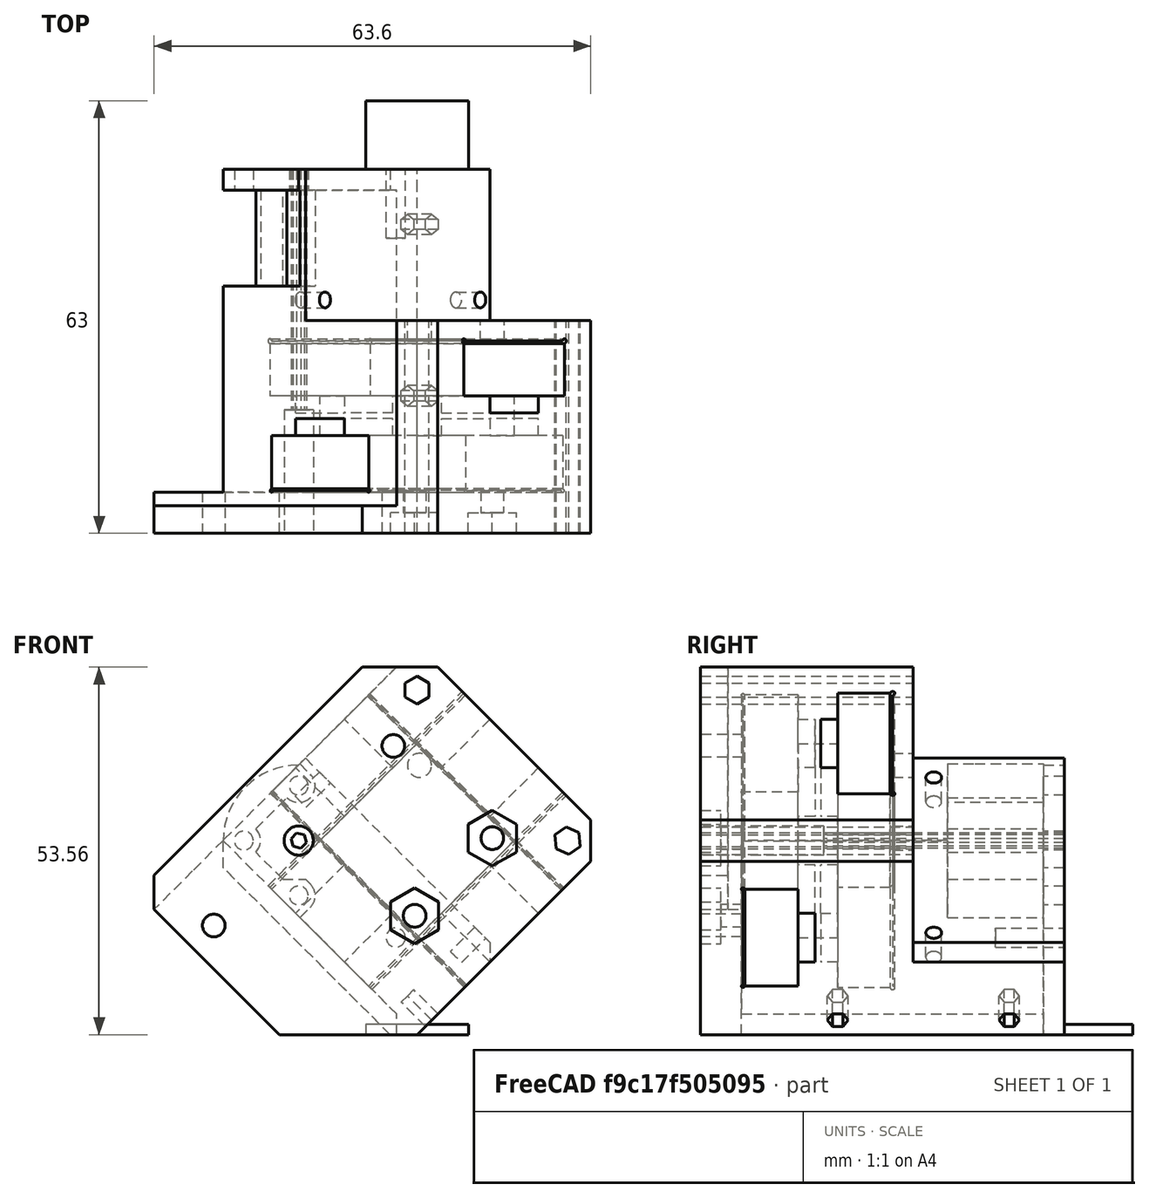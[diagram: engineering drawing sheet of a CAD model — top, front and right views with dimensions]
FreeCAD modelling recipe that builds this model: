
FCSTD DOCUMENT  (FreeCAD 0.19R)
Label: Top
License: All rights reserved
LicenseURL: http://en.wikipedia.org/wiki/All_rights_reserved
objects: Sketcher::SketchObject×25, PartDesign::Pocket×18, PartDesign::Pad×5, PartDesign::Body×1, Mesh::Feature×1
note: 72 computed .brp shape members not serialized (recipe doc carries the construction recipe); baked Part::Feature solids carry a one-line shape summary decoded from their .brp

FEATURE [Sketcher::SketchObject] Sketch  label="Body001"
  FullyConstrained = true
  MapMode = 5
  Support = -> [XY_Plane]
  sketch-geometry (11):
    g0: LineSegment StartX=20 StartY=15.7574 StartZ=0 EndX=20 EndY=-15.7574 EndZ=0
    g1: LineSegment StartX=15.7574 StartY=-20 StartZ=0 EndX=-20 EndY=-20 EndZ=0
    g2: LineSegment StartX=-20 StartY=-15.7574 StartZ=0 EndX=-20 EndY=19.9515 EndZ=0
    g3: Circle CenterX=-12.1976 CenterY=12.1976 CenterZ=0 NormalX=0 NormalY=0 NormalZ=1 AngleXU=0 Radius=2.1
    g4: LineSegment StartX=-12.1976 StartY=12.1976 StartZ=0 EndX=0 EndY=0 EndZ=0
    g5: ArcOfCircle CenterX=-12.1976 CenterY=12.1976 CenterZ=0 NormalX=0 NormalY=0 NormalZ=1 AngleXU=0 Radius=11 StartAngle=0.788519 EndAngle=2.35931
    g6: LineSegment StartX=-4.44373 StartY=20 StartZ=0 EndX=15.7574 EndY=20 EndZ=0
    g7: LineSegment StartX=15.7574 StartY=-20 StartZ=0 EndX=20 EndY=-15.7574 EndZ=0
    g8: LineSegment StartX=-20 StartY=-15.7574 StartZ=0 EndX=-22.1213 EndY=-17.8787 EndZ=0
    g9: LineSegment StartX=-22.1213 StartY=-17.8787 StartZ=0 EndX=-20 EndY=-20 EndZ=0
    g10: LineSegment StartX=15.7574 StartY=20 StartZ=0 EndX=20 EndY=15.7574 EndZ=0
  constraints (32):
    c: Horizontal(g1)
    c: Vertical(g0)
    c: Vertical(g2)
    c: Distance(g-1,g3) = 17.25
    c: Coincident(g4,g3)
    c: Coincident(g4,g-1)
    c: Angle(g4) = -0.785398
    c: Diameter(g3) = 4.2
    c: Coincident(g5,g3)
    c: Diameter(g5) = 22
    c: DistanceX(g1) = -20
    c: Coincident(g6,g5)
    c: Horizontal(g6)
    c: Coincident(g5,g2)
    c: Coincident(g7,g1)
    c: Coincident(g7,g0)
    c: Angle(g7) = 0.785398
    c: Distance(g7) = 6
    c: DistanceY(g1) = -20
    c: Coincident(g2,g8)
    c: Coincident(g8,g9)
    c: Coincident(g9,g1)
    c: Angle(g9) = -0.785398
    c: Angle(g8) = -2.35619
    c: Distance(g9) = 3
    c: DistanceX(g2) = -20
    c: Coincident(g10,g6)
    c: Coincident(g10,g0)
    c: Distance(g10) = 6
    c: Angle(g10) = -0.785398
    c: DistanceX(g0) = 20
    c: DistanceY(g6) = 20
FEATURE [PartDesign::Pad] Pad
  Direction = (1,1,1)
  Length = 53
  Length2 = 10
  Profile = -> Sketch
  Reversed = true
  Type = 0
FEATURE [Sketcher::SketchObject] Sketch001  label="RailHole"
  FullyConstrained = true
  MapMode = 5
  Placement = pos=(20,0,0) rot=(0.57735,0.57735,0.57735;2.0944rad)
  Support = -> [Pad]
  sketch-geometry (10):
    g0: LineSegment StartX=-10.35 StartY=-27.65 StartZ=0 EndX=-10.35 EndY=-20 EndZ=0
    g1: LineSegment StartX=5 StartY=-17.5 StartZ=0 EndX=-5 EndY=-17.5 EndZ=0
    g2: LineSegment StartX=10 StartY=-28 StartZ=0 EndX=-10 EndY=-28 EndZ=0
    g3: LineSegment StartX=5 StartY=-17.5 StartZ=0 EndX=5 EndY=-20 EndZ=0
    g4: LineSegment StartX=-5 StartY=-20 StartZ=0 EndX=-5 EndY=-17.5 EndZ=0
    g5: LineSegment StartX=-10.35 StartY=-20 StartZ=0 EndX=-5 EndY=-20 EndZ=0
    g6: LineSegment StartX=5 StartY=-20 StartZ=0 EndX=10.3495 EndY=-20 EndZ=0
    g7: LineSegment StartX=10.3495 StartY=-27.65 StartZ=0 EndX=10.3495 EndY=-20 EndZ=0
    g8: ArcOfCircle CenterX=-10.35 CenterY=-28 CenterZ=0 NormalX=0 NormalY=0 NormalZ=1 AngleXU=0 Radius=0.35 StartAngle=1.5708 EndAngle=6.28319
    g9: ArcOfCircle CenterX=10.35 CenterY=-28 CenterZ=0 NormalX=0 NormalY=0 NormalZ=1 AngleXU=0 Radius=0.35 StartAngle=3.14159 EndAngle=7.85541
  constraints (29):
    c: Vertical(g0)
    c: Symmetric(g1,g1,g-2)
    c: Distance(g1) = 10
    c: Coincident(g1,g3)
    c: Vertical(g3)
    c: Coincident(g4,g1)
    c: Symmetric(g3,g4,g-2)
    c: Distance(g3) = 2.5
    c: Distance(g2) = 20
    c: Coincident(g5,g4)
    c: Horizontal(g5)
    c: Coincident(g3,g6)
    c: Horizontal(g6)
    c: Vertical(g7)
    c: Coincident(g0,g5)
    c: Coincident(g7,g6)
    c: Coincident(g0,g8)
    c: Coincident(g8,g2)
    c: Diameter(g8) = 0.7
    c: DistanceX(g0,g8) = 0
    c: DistanceY(g2,g8) = 0
    c: Coincident(g9,g2)
    c: Coincident(g9,g7)
    c: Diameter(g9) = 0.7
    c: DistanceY(g2,g9) = 0
    c: DistanceX(g7,g9) = 0.0005
    c: Symmetric(g9,g8,g-2)
    c: Distance(g9,g6) = 8
    c: DistanceY(g8) = -28
FEATURE [PartDesign::Pocket] Pocket
  BaseFeature = -> Pad
  Length = 5
  Length2 = 100
  Profile = -> Sketch001
  Type = 1
FEATURE [Sketcher::SketchObject] Sketch008  label="ExtruderHole"
  FullyConstrained = false
  MapMode = 5
  Placement = pos=(0,0,4) rot=(0,0,1;0rad)
  sketch-geometry (2):
    g0: LineSegment StartX=0 StartY=0 StartZ=0 EndX=-54.6242 EndY=54.6242 EndZ=0
    g1: Circle CenterX=-12.1976 CenterY=12.1976 CenterZ=0 NormalX=0 NormalY=0 NormalZ=1 AngleXU=0 Radius=0.75
  constraints (5):
    c: Coincident(g0,g-1)
    c: Angle(g0) = 2.35619
    c: PointOnObject(g1,g0)
    c: Distance(g-1,g1) = 17.25
    c: Diameter(g1) = 1.5
FEATURE [Sketcher::SketchObject] Sketch009  label="reference"
  FullyConstrained = false
  MapMode = 5
  Placement = pos=(0,0,-25) rot=(1,0,0;3.14159rad)
  sketch-geometry (2):
    g0: Circle CenterX=-12.0208 CenterY=-12.0208 CenterZ=0 NormalX=0 NormalY=0 NormalZ=1 AngleXU=0 Radius=10
    g1: LineSegment StartX=0 StartY=0 StartZ=0 EndX=-27.7674 EndY=-27.7674 EndZ=0
  constraints (5):
    c: Diameter(g0) = 20
    c: Coincident(g1,g-1)
    c: Angle(g1) = -2.35619
    c: PointOnObject(g0,g1)
    c: Distance(g0,g1) = 17
FEATURE [Sketcher::SketchObject] Sketch010  label="reference2"
  FullyConstrained = false
  MapMode = 5
  Placement = pos=(0,0,-37) rot=(1,0,0;3.14159rad)
  sketch-geometry (2):
    g0: Circle CenterX=-12.1976 CenterY=-12.1976 CenterZ=0 NormalX=0 NormalY=0 NormalZ=1 AngleXU=0 Radius=8
    g1: LineSegment StartX=0 StartY=0 StartZ=0 EndX=-38.1566 EndY=-38.1566 EndZ=0
  constraints (5):
    c: Diameter(g0) = 16
    c: Coincident(g1,g-1)
    c: Angle(g1) = -2.35619
    c: Distance(g0,g1) = 17.25
    c: PointOnObject(g0,g1)
FEATURE [Sketcher::SketchObject] Sketch021  label="InternalTri"
  FullyConstrained = true
  MapMode = 5
  Placement = pos=(0,-3e-15,-12) rot=(0,0,1;0rad)
  sketch-geometry (4):
    g0: LineSegment StartX=-10 StartY=10 StartZ=0 EndX=10 EndY=10 EndZ=0
    g1: LineSegment StartX=10 StartY=10 StartZ=0 EndX=10 EndY=-10 EndZ=0
    g2: LineSegment StartX=10 StartY=-10 StartZ=0 EndX=-10 EndY=-10 EndZ=0
    g3: LineSegment StartX=-10 StartY=-10 StartZ=0 EndX=-10 EndY=10 EndZ=0
  constraints (11):
    c: Coincident(g0,g1)
    c: Coincident(g1,g2)
    c: Coincident(g2,g3)
    c: Coincident(g3,g0)
    c: Horizontal(g0)
    c: Horizontal(g2)
    c: Vertical(g1)
    c: Vertical(g3)
    c: Symmetric(g1,g0,g-1)
    c: Equal(g1,g0)
    c: Distance(g1) = 20
FEATURE [PartDesign::Pocket] Pocket002
  BaseFeature = -> Pocket
  Length = 10
  Length2 = 2
  Profile = -> Sketch021
  Type = 4
FEATURE [Sketcher::SketchObject] Sketch019  label="RailHole2"
  FullyConstrained = true
  MapMode = 5
  Placement = pos=(0,-20,0) rot=(1,0,0;1.5708rad)
  Support = -> [Pocket002]
  sketch-geometry (10):
    g0: LineSegment StartX=-9.75 StartY=-6.2 StartZ=0 EndX=9.75 EndY=-6.2 EndZ=0
    g1: LineSegment StartX=10 StartY=-14.2 StartZ=0 EndX=5 EndY=-14.2 EndZ=0
    g2: LineSegment StartX=5 StartY=-14.2 StartZ=0 EndX=5 EndY=-16.7 EndZ=0
    g3: LineSegment StartX=5 StartY=-16.7 StartZ=0 EndX=-5 EndY=-16.7 EndZ=0
    g4: LineSegment StartX=-5 StartY=-16.7 StartZ=0 EndX=-5 EndY=-14.2 EndZ=0
    g5: LineSegment StartX=-5 StartY=-14.2 StartZ=0 EndX=-10 EndY=-14.2 EndZ=0
    g6: ArcOfCircle CenterX=10 CenterY=-6.2 CenterZ=0 NormalX=0 NormalY=0 NormalZ=1 AngleXU=0 Radius=0.25 StartAngle=4.71239 EndAngle=9.42478
    g7: ArcOfCircle CenterX=-10 CenterY=-6.2 CenterZ=0 NormalX=0 NormalY=0 NormalZ=1 AngleXU=0 Radius=0.25 StartAngle=-9e-16 EndAngle=4.71239
    g8: LineSegment StartX=-10 StartY=-14.2 StartZ=0 EndX=-10 EndY=-6.45 EndZ=0
    g9: LineSegment StartX=10 StartY=-14.2 StartZ=0 EndX=10 EndY=-6.45 EndZ=0
  constraints (29):
    c: Horizontal(g0)
    c: Horizontal(g1)
    c: Coincident(g1,g2)
    c: Vertical(g2)
    c: Coincident(g2,g3)
    c: Horizontal(g3)
    c: Coincident(g3,g4)
    c: Vertical(g4)
    c: Coincident(g4,g5)
    c: Symmetric(g1,g5,g-2)
    c: Distance(g3) = 10
    c: Symmetric(g4,g1,g-2)
    c: DistanceY(g0) = -6.2
    c: Distance(g2) = 2.5
    c: Coincident(g6,g0)
    c: Coincident(g7,g0)
    c: Distance(g7,g6) = 20
    c: DistanceY(g1,g6) = 8
    c: Coincident(g8,g5)
    c: Vertical(g8)
    c: Coincident(g9,g1)
    c: Coincident(g9,g6)
    c: Vertical(g9)
    c: Coincident(g7,g8)
    c: Symmetric(g6,g7,g-2)
    c: Diameter(g6) = 0.5
    c: Equal(g6,g7)
    c: DistanceX(g7,g7) = 0
    c: DistanceY(g7,g0) = 0
FEATURE [Sketcher::SketchObject] Sketch024  label="hgxLITEholes"
  FullyConstrained = false
  MapMode = 5
  Placement = pos=(0,0,4) rot=(0,0,1;0rad)
  sketch-geometry (5):
    g0: Circle CenterX=7.30241 CenterY=12.1976 CenterZ=0 NormalX=0 NormalY=0 NormalZ=1 AngleXU=0 Radius=1.65
    g1: Circle CenterX=-29.6976 CenterY=12.1976 CenterZ=0 NormalX=0 NormalY=0 NormalZ=1 AngleXU=0 Radius=1.65
    g2: LineSegment StartX=-29.6976 StartY=12.1976 StartZ=0 EndX=7.30241 EndY=12.1976 EndZ=0
    g3: LineSegment StartX=0 StartY=0 StartZ=0 EndX=-27.1729 EndY=27.1729 EndZ=0
    g4: Circle CenterX=-12.1976 CenterY=12.1976 CenterZ=0 NormalX=0 NormalY=0 NormalZ=1 AngleXU=0 Radius=1.0154
  constraints (12):
    c: Diameter(g0) = 3.3
    c: Equal(g0,g1)
    c: Coincident(g2,g1)
    c: Coincident(g2,g0)
    c: Distance(g2) = 37
    c: Coincident(g3,g-1)
    c: Angle(g3) = 2.35619
    c: PointOnObject(g4,g3)
    c: Distance(g-1,g4) = 17.25
    c: Distance(g4,g0) = 19.5
    c: Horizontal(g2)
    c: PointOnObject(g4,g2)
FEATURE [PartDesign::Pocket] Pocket003
  BaseFeature = -> Pocket002
  Length = 5
  Length2 = 100
  Profile = -> Sketch019
  Type = 1
FEATURE [Sketcher::SketchObject] Sketch026  label="BottomSculp"
  FullyConstrained = false
  MapMode = 5
  Placement = pos=(0,0,-53) rot=(1,0,0;3.14159rad)
  Support = -> [Pocket003]
  sketch-geometry (5):
    g0: LineSegment StartX=29.4648 StartY=27.8981 StartZ=0 EndX=28.2209 EndY=-23.4245 EndZ=0
    g1: LineSegment StartX=28.2209 StartY=-23.4245 StartZ=0 EndX=-3.00001 EndY=-23.4245 EndZ=0
    g2: LineSegment StartX=-3.00001 StartY=-23.4245 StartZ=0 EndX=-3 EndY=18 EndZ=0
    g3: LineSegment StartX=-3 StartY=18 StartZ=0 EndX=-14.2101 EndY=29.2101 EndZ=0
    g4: LineSegment StartX=-14.2101 StartY=29.2101 StartZ=0 EndX=29.4648 EndY=27.8981 EndZ=0
  constraints (11):
    c: Coincident(g0,g1)
    c: Horizontal(g1)
    c: Coincident(g1,g2)
    c: Angle(g2) = 1.5708
    c: Coincident(g2,g3)
    c: Angle(g3) = 2.35619
    c: Coincident(g4,g3)
    c: Coincident(g4,g0)
    c: DistanceY(g2) = 18
    c: DistanceX(g2) = -3
    c: Angle(g3) = 2.35619
FEATURE [PartDesign::Pocket] Pocket004
  BaseFeature = -> Pocket003
  Length = 22
  Length2 = 100
  Profile = -> Sketch026
  Type = 0
FEATURE [Sketcher::SketchObject] Sketch004  label="Yboltpattern"
  FullyConstrained = true
  MapMode = 5
  Placement = pos=(0,0,-31) rot=(1,0,0;3.14159rad)
  Support = -> [Pocket004]
  sketch-geometry (8):
    g0: Circle CenterX=-8 CenterY=7.5 CenterZ=0 NormalX=0 NormalY=0 NormalZ=1 AngleXU=0 Radius=1.75
    g1: Circle CenterX=8 CenterY=7.5 CenterZ=0 NormalX=0 NormalY=0 NormalZ=1 AngleXU=0 Radius=1.75
    g2: Circle CenterX=-8 CenterY=-7.5 CenterZ=0 NormalX=0 NormalY=0 NormalZ=1 AngleXU=0 Radius=1.75
    g3: Circle CenterX=8 CenterY=-7.5 CenterZ=0 NormalX=0 NormalY=0 NormalZ=1 AngleXU=0 Radius=1.75
    g4: LineSegment StartX=-8 StartY=7.5 StartZ=0 EndX=8 EndY=7.5 EndZ=0
    g5: LineSegment StartX=8 StartY=7.5 StartZ=0 EndX=8 EndY=-7.5 EndZ=0
    g6: LineSegment StartX=8 StartY=-7.5 StartZ=0 EndX=-8 EndY=-7.5 EndZ=0
    g7: LineSegment StartX=-8 StartY=-7.5 StartZ=0 EndX=-8 EndY=7.5 EndZ=0
  constraints (18):
    c: Diameter(g0) = 3.5
    c: Equal(g0,g1)
    c: Equal(g0,g2)
    c: Equal(g0,g3)
    c: Distance(g2,g0) = 15
    c: Distance(g3,g2) = 16
    c: Coincident(g4,g0)
    c: Coincident(g4,g1)
    c: Coincident(g4,g5)
    c: Coincident(g5,g3)
    c: Coincident(g5,g6)
    c: Coincident(g6,g2)
    c: Coincident(g6,g7)
    c: Coincident(g7,g4)
    c: Equal(g5,g7)
    c: Equal(g4,g6)
    c: Symmetric(g1,g2,g-1)
    c: Symmetric(g0,g1,g-2)
FEATURE [Sketcher::SketchObject] Sketch022  label="VoronHoleRelif"
  FullyConstrained = true
  MapMode = 5
  Placement = pos=(0,0,-28) rot=(0,0,1;0rad)
  Support = -> [Pocket004]
  sketch-geometry (11):
    g0: ArcOfCircle CenterX=-17.8884 CenterY=6.52425 CenterZ=0 NormalX=0 NormalY=0 NormalZ=1 AngleXU=0 Radius=2.4 StartAngle=4.71239 EndAngle=6.28319
    g1: ArcOfCircle CenterX=-6.58192 CenterY=17.8307 CenterZ=0 NormalX=0 NormalY=0 NormalZ=1 AngleXU=0 Radius=2.4 StartAngle=3.14159 EndAngle=6.28319
    g2: LineSegment StartX=-22.2684 StartY=4.12425 StartZ=0 EndX=-17.8884 EndY=4.12425 EndZ=0
    g3: LineSegment StartX=-22.2684 StartY=23.8307 StartZ=0 EndX=-4.18192 EndY=23.8307 EndZ=0
    g4: LineSegment StartX=-4.18192 StartY=23.8307 StartZ=0 EndX=-4.18192 EndY=17.8307 EndZ=0
    g5: LineSegment StartX=-22.2684 StartY=4.12425 StartZ=0 EndX=-22.2684 EndY=23.8307 EndZ=0
    g6: ArcOfCircle CenterX=-17.8172 CenterY=17.8307 CenterZ=0 NormalX=0 NormalY=0 NormalZ=1 AngleXU=0 Radius=2.4 StartAngle=4.71239 EndAngle=6.28319
    g7: LineSegment StartX=-15.4172 StartY=17.8307 StartZ=0 EndX=-8.98192 EndY=17.8307 EndZ=0
    g8: LineSegment StartX=-17.8172 StartY=9.85307 StartZ=0 EndX=-15.4884 EndY=7.52425 EndZ=0
    g9: LineSegment StartX=-15.4884 StartY=6.52425 StartZ=0 EndX=-15.4884 EndY=7.52425 EndZ=0
    g10: LineSegment StartX=-17.8172 StartY=9.85307 StartZ=0 EndX=-17.8172 EndY=15.4307 EndZ=0
  constraints (33):
    c: Horizontal(g2)
    c: Coincident(g3,g4)
    c: Tangent(g4,g1) = 1.5708
    c: Tangent(g2,g0) = -1.5708
    c: Diameter(g0) = 4.8
    c: Equal(g0,g1)
    c: Vertical(g4)
    c: Horizontal(g3)
    c: Coincident(g5,g2)
    c: Coincident(g5,g3)
    c: Vertical(g5)
    c: Distance(g2) = 4.38
    c: Distance(g4) = 6
    c: DistanceX(g1) = -6.58192
    c: DistanceY(g1) = 17.8307
    c: DistanceX(g0) = -17.8884
    c: DistanceY(g0) = 6.52425
    c: Coincident(g7,g6)
    c: Coincident(g7,g1)
    c: Horizontal(g7)
    c: Perpendicular(g1,g7)
    c: Diameter(g6) = 4.8
    c: Perpendicular(g6,g7)
    c: Angle(g8) = -0.785398
    c: Vertical(g9)
    c: Tangent(g9,g0) = -1.5708
    c: Distance(g9) = 1
    c: Coincident(g8,g9)
    c: Coincident(g10,g8)
    c: Coincident(g10,g6)
    c: Vertical(g10)
    c: Perpendicular(g6,g10)
    c: DistanceX(g6) = -17.8172
FEATURE [PartDesign::Pocket] Pocket005
  BaseFeature = -> Pocket004
  Length = 22
  Length2 = -8
  Profile = -> Sketch022
  Type = 4
FEATURE [Sketcher::SketchObject] Sketch017  label="VoronHoles3"
  FullyConstrained = true
  MapMode = 5
  Placement = pos=(0,0,-50) rot=(0,0,1;0rad)
  Support = -> [Pocket005]
  sketch-geometry (10):
    g0: Circle CenterX=-6.54074 CenterY=17.8544 CenterZ=0 NormalX=0 NormalY=0 NormalZ=1 AngleXU=0 Radius=1.375
    g1: Circle CenterX=-17.8544 CenterY=6.54074 CenterZ=0 NormalX=0 NormalY=0 NormalZ=1 AngleXU=0 Radius=1.375
    g2: Circle CenterX=-6.54074 CenterY=6.54074 CenterZ=0 NormalX=0 NormalY=0 NormalZ=1 AngleXU=0 Radius=1.375
    g3: Circle CenterX=-17.8544 CenterY=17.8544 CenterZ=0 NormalX=0 NormalY=0 NormalZ=1 AngleXU=0 Radius=1.375
    g4: LineSegment StartX=-6.54074 StartY=17.8544 StartZ=0 EndX=-6.54074 EndY=6.54074 EndZ=0
    g5: LineSegment StartX=-6.54074 StartY=6.54074 StartZ=0 EndX=-17.8544 EndY=6.54074 EndZ=0
    g6: LineSegment StartX=-17.8544 StartY=6.54074 StartZ=0 EndX=-17.8544 EndY=17.8544 EndZ=0
    g7: LineSegment StartX=-17.8544 StartY=17.8544 StartZ=0 EndX=-6.54074 EndY=17.8544 EndZ=0
    g8: LineSegment StartX=0 StartY=0 StartZ=0 EndX=-37.1726 EndY=37.1726 EndZ=0
    g9: Circle CenterX=-12.1976 CenterY=12.1976 CenterZ=0 NormalX=0 NormalY=0 NormalZ=1 AngleXU=0 Radius=0.77
  constraints (25):
    c: Coincident(g4,g0)
    c: Coincident(g4,g2)
    c: Coincident(g4,g5)
    c: Coincident(g5,g1)
    c: Coincident(g5,g6)
    c: Coincident(g6,g3)
    c: Coincident(g6,g7)
    c: Coincident(g7,g4)
    c: Equal(g4,g7)
    c: Equal(g7,g6)
    c: Equal(g6,g5)
    c: Coincident(g8,g-1)
    c: PointOnObject(g9,g8)
    c: Distance(g-1,g9) = 17.25
    c: Diameter(g1) = 2.75
    c: Equal(g1,g3)
    c: Equal(g1,g0)
    c: Equal(g1,g2)
    c: Symmetric(g0,g1,g9)
    c: Distance(g2,g3) = 16
    c: Angle(g8) = 2.35619
    c: PointOnObject(g2,g8)
    c: Perpendicular(g7,g4)
    c: Distance(g8) = 52.57
    c: Diameter(g9) = 1.54
FEATURE [PartDesign::Pocket] Pocket006
  BaseFeature = -> Pocket005
  Length = 5
  Length2 = 100
  Profile = -> Sketch017
  Type = 1
FEATURE [Sketcher::SketchObject] Sketch025  label="FanDuctMountHole"
  FullyConstrained = true
  MapMode = 5
  Placement = pos=(0,0,-53) rot=(1,0,0;3.14159rad)
  Support = -> [Pocket006]
  sketch-geometry (1):
    g0: Circle CenterX=-12.2 CenterY=7.8 CenterZ=0 NormalX=0 NormalY=0 NormalZ=1 AngleXU=0 Radius=1.4
  constraints (3):
    c: Diameter(g0) = 2.8
    c: DistanceX(g0) = -12.2
    c: DistanceY(g0) = 7.8
FEATURE [PartDesign::Pocket] Pocket007
  BaseFeature = -> Pocket006
  Length = 10
  Length2 = 100
  Profile = -> Sketch025
  Type = 0
FEATURE [PartDesign::Pocket] Pocket008
  BaseFeature = -> Pocket007
  Length = 9
  Length2 = 100
  Profile = -> Sketch004
  Type = 0
FEATURE [Sketcher::SketchObject] Sketch007  label="ExtruderPlatform"
  ExternalGeometry = -> [Pad]
  FullyConstrained = false
  MapMode = 5
  Support = -> [Pocket008]
  sketch-geometry (12):
    g0: LineSegment StartX=-20 StartY=-20 StartZ=0 EndX=15.7574 EndY=-20 EndZ=0
    g1: LineSegment StartX=0 StartY=0 StartZ=0 EndX=-70.7107 EndY=70.7107 EndZ=0
    g2: Circle CenterX=-12.1976 CenterY=12.1976 CenterZ=0 NormalX=0 NormalY=0 NormalZ=1 AngleXU=0 Radius=2.125
    g3: LineSegment StartX=15.7574 StartY=-20 StartZ=0 EndX=20 EndY=-15.7574 EndZ=0
    g4: LineSegment StartX=20 StartY=-15.7574 StartZ=0 EndX=20 EndY=15.7574 EndZ=0
    g5: LineSegment StartX=20 StartY=15.7574 StartZ=0 EndX=15.7574 EndY=20 EndZ=0
    g6: LineSegment StartX=-20 StartY=-20 StartZ=0 EndX=-34.1976 EndY=-5.80241 EndZ=0
    g7: LineSegment StartX=-12.1976 StartY=-100 StartZ=0 EndX=-12.1976 EndY=100 EndZ=0
    g8: LineSegment StartX=-34.1976 StartY=-5.80241 StartZ=0 EndX=-34.1976 EndY=20 EndZ=0
    g9: LineSegment StartX=-34.1976 StartY=20 StartZ=0 EndX=15.7574 EndY=20 EndZ=0
    g10: Circle CenterX=-29.6976 CenterY=12.1976 CenterZ=0 NormalX=0 NormalY=0 NormalZ=1 AngleXU=0 Radius=1.4
    g11: Circle CenterX=7.30241 CenterY=11.9057 CenterZ=0 NormalX=0 NormalY=0 NormalZ=1 AngleXU=0 Radius=1.4
  constraints (35):
    c: Coincident(g1,g-1)
    c: Angle(g1) = 2.35619
    c: Diameter(g2) = 4.25
    c: PointOnObject(g2,g1)
    c: Distance(g-1,g2) = 17.25
    c: Coincident(g0,g3)
    c: Coincident(g3,g4)
    c: Coincident(g6,g0)
    c: Angle(g6) = 2.35619
    c: Coincident(g5,g4)
    c: Distance(g1) = 100
    c: PointOnObject(g2,g7)
    c: DistanceX(g0,g0) = -35.7574
    c: DistanceY(g0,g0) = 0
    c: DistanceX(g3,g0) = -40
    c: DistanceY(g3,g0) = -4.24264
    c: DistanceX(g4) = 20
    c: DistanceY(g4) = 15.7574
    c: DistanceX(g3) = 20
    c: DistanceY(g3) = -15.7574
    c: Coincident(g8,g6)
    c: Vertical(g8)
    c: Horizontal(g9)
    c: Coincident(g5,g9)
    c: Distance(g8,g7) = 22
    c: DistanceX(g5) = 15.7574
    c: DistanceY(g5) = 20
    c: Symmetric(g7,g7,g-1)
    c: Distance(g7) = 200
    c: DistanceX(g10,g2) = 17.5
    c: DistanceX(g2,g11) = 19.5
    c: Diameter(g10) = 2.8
    c: Equal(g10,g11)
    c: DistanceY(g10,g2) = 0
    c: Coincident(g9,g8)
FEATURE [PartDesign::Pad] Pad001
  BaseFeature = -> Pocket008
  Direction = (1,1,1)
  Length = 6
  Length2 = 100
  Profile = -> Sketch007
  Reversed = true
  Type = 0
FEATURE [PartDesign::Pocket] Pocket009
  BaseFeature = -> Pad001
  Length = 11
  Length2 = 100
  Profile = -> Sketch024
  Type = 0
FEATURE [PartDesign::Pocket] Pocket010
  BaseFeature = -> Pocket009
  Length = 5
  Length2 = 100
  Profile = -> Sketch008
  Type = 1
FEATURE [Sketcher::SketchObject] Sketch003  label="Xboltpattern"
  FullyConstrained = true
  MapMode = 5
  Support = -> [Pocket010]
  sketch-geometry (8):
    g0: Circle CenterX=-8 CenterY=7.5 CenterZ=0 NormalX=0 NormalY=0 NormalZ=1 AngleXU=0 Radius=1.65
    g1: Circle CenterX=8 CenterY=7.5 CenterZ=0 NormalX=0 NormalY=0 NormalZ=1 AngleXU=0 Radius=1.65
    g2: Circle CenterX=-8 CenterY=-7.5 CenterZ=0 NormalX=0 NormalY=0 NormalZ=1 AngleXU=0 Radius=1.65
    g3: Circle CenterX=8 CenterY=-7.5 CenterZ=0 NormalX=0 NormalY=0 NormalZ=1 AngleXU=0 Radius=1.65
    g4: LineSegment StartX=-8 StartY=7.5 StartZ=0 EndX=8 EndY=7.5 EndZ=0
    g5: LineSegment StartX=8 StartY=7.5 StartZ=0 EndX=8 EndY=-7.5 EndZ=0
    g6: LineSegment StartX=8 StartY=-7.5 StartZ=0 EndX=-8 EndY=-7.5 EndZ=0
    g7: LineSegment StartX=-8 StartY=-7.5 StartZ=0 EndX=-8 EndY=7.5 EndZ=0
  constraints (19):
    c: Diameter(g0) = 3.3
    c: Equal(g0,g1)
    c: Equal(g0,g2)
    c: Equal(g0,g3)
    c: Distance(g0,g1) = 16
    c: Distance(g1,g3) = 15
    c: Coincident(g4,g0)
    c: Coincident(g4,g1)
    c: Horizontal(g4)
    c: Coincident(g4,g5)
    c: Coincident(g5,g3)
    c: Vertical(g5)
    c: Coincident(g5,g6)
    c: Coincident(g6,g2)
    c: Coincident(g6,g7)
    c: Coincident(g7,g4)
    c: Symmetric(g2,g1,g-1)
    c: Equal(g7,g5)
    c: Equal(g6,g4)
FEATURE [Sketcher::SketchObject] Sketch029  label="Adhesion"
  FullyConstrained = false
  MapMode = 5
  Placement = pos=(0,0,-53) rot=(1,0,0;3.14159rad)
  sketch-geometry (4):
    g0: LineSegment StartX=-13.636 StartY=24.2426 StartZ=0 EndX=-24.2426 EndY=13.636 EndZ=0
    g1: LineSegment StartX=-24.2426 StartY=13.636 StartZ=0 EndX=-25.3033 EndY=14.6967 EndZ=0
    g2: LineSegment StartX=-25.3033 StartY=14.6967 StartZ=0 EndX=-14.6967 EndY=25.3033 EndZ=0
    g3: LineSegment StartX=-14.6967 StartY=25.3033 StartZ=0 EndX=-13.636 EndY=24.2426 EndZ=0
  constraints (10):
    c: Coincident(g0,g1)
    c: Coincident(g1,g2)
    c: Coincident(g2,g3)
    c: Coincident(g3,g0)
    c: Angle(g2) = 0.785398
    c: Distance(g2) = 15
    c: Distance(g1) = 1.5
    c: Distance(g3) = 1.5
    c: Perpendicular(g2,g3)
    c: Perpendicular(g2,g1)
FEATURE [Sketcher::SketchObject] Sketch033  label="WireMgmnt"
  FullyConstrained = true
  MapMode = 5
  Placement = pos=(0,-20,0) rot=(1,0,0;1.5708rad)
  sketch-geometry (14):
    g0: LineSegment StartX=-15.7 StartY=-20.7506 StartZ=0 EndX=-15.7 EndY=-19.2494 EndZ=0
    g1: LineSegment StartX=-15.7 StartY=-19.2494 StartZ=0 EndX=-17 EndY=-18.4989 EndZ=0
    g2: LineSegment StartX=-17 StartY=-18.4989 StartZ=0 EndX=-18.3 EndY=-19.2494 EndZ=0
    g3: LineSegment StartX=-18.3 StartY=-19.2494 StartZ=0 EndX=-18.3 EndY=-20.7506 EndZ=0
    g4: LineSegment StartX=-18.3 StartY=-20.7506 StartZ=0 EndX=-17 EndY=-21.5011 EndZ=0
    g5: LineSegment StartX=-17 StartY=-21.5011 StartZ=0 EndX=-15.7 EndY=-20.7506 EndZ=0
    g6: Circle CenterX=-17 CenterY=-20 CenterZ=0 NormalX=0 NormalY=0 NormalZ=1 AngleXU=0 Radius=1.50111
    g7: LineSegment StartX=-15.7 StartY=-44.2494 StartZ=0 EndX=-17 EndY=-43.4989 EndZ=0
    g8: LineSegment StartX=-17 StartY=-43.4989 StartZ=0 EndX=-18.3 EndY=-44.2494 EndZ=0
    g9: LineSegment StartX=-18.3 StartY=-44.2494 StartZ=0 EndX=-18.3 EndY=-45.7506 EndZ=0
    g10: LineSegment StartX=-18.3 StartY=-45.7506 StartZ=0 EndX=-17 EndY=-46.5011 EndZ=0
    g11: LineSegment StartX=-17 StartY=-46.5011 StartZ=0 EndX=-15.7 EndY=-45.7506 EndZ=0
    g12: LineSegment StartX=-15.7 StartY=-45.7506 StartZ=0 EndX=-15.7 EndY=-44.2494 EndZ=0
    g13: Circle CenterX=-17 CenterY=-45 CenterZ=0 NormalX=0 NormalY=0 NormalZ=1 AngleXU=0 Radius=1.50111
  constraints (34):
    c: Coincident(g0,g1)
    c: Coincident(g1,g2)
    c: Coincident(g2,g3)
    c: Coincident(g3,g4)
    c: Coincident(g4,g5)
    c: Coincident(g5,g0)
    c: Equal(g0, g1-g5) x5
    c: PointOnObject(g0,g6)
    c: PointOnObject(g1,g6)
    c: PointOnObject(g2,g6)
    c: PointOnObject(g3,g6)
    c: PointOnObject(g4,g6)
    c: PointOnObject(g5,g6)
    c: Coincident(g7,g8)
    c: Coincident(g8,g9)
    c: Coincident(g9,g10)
    c: Coincident(g10,g11)
    c: Coincident(g11,g12)
    c: Coincident(g12,g7)
    c: Equal(g7, g8-g12) x5
    c: PointOnObject(g7,g13)
    c: PointOnObject(g8,g13)
    c: PointOnObject(g9,g13)
    c: PointOnObject(g10,g13)
    c: PointOnObject(g11,g13)
    c: PointOnObject(g12,g13)
    c: DistanceX(g13) = -17
    c: Distance(g10,g7) = 2.6
    c: Vertical(g9)
    c: DistanceY(g13) = -45
    c: Distance(g3,g0) = 2.6
    c: DistanceY(g6) = -20
    c: Vertical(g3)
    c: DistanceX(g6) = -17
FEATURE [Sketcher::SketchObject] Sketch035  label="Bottom Reinforce"
  FullyConstrained = false
  MapMode = 5
  Placement = pos=(0,0,-53) rot=(1,0,0;3.14159rad)
  sketch-geometry (4):
    g0: LineSegment StartX=-22.779 StartY=17.221 StartZ=0 EndX=-22.779 EndY=-17.1725 EndZ=0
    g1: LineSegment StartX=-22.779 StartY=-17.1725 StartZ=0 EndX=-20 EndY=-19.9515 EndZ=0
    g2: LineSegment StartX=-20 StartY=-19.9515 StartZ=0 EndX=-20 EndY=20 EndZ=0
    g3: LineSegment StartX=-20 StartY=20 StartZ=0 EndX=-22.779 EndY=17.221 EndZ=0
  constraints (9):
    c: Vertical(g0)
    c: Coincident(g0,g1)
    c: Coincident(g1,g2)
    c: Vertical(g2)
    c: Coincident(g2,g3)
    c: Coincident(g3,g0)
    c: Angle(g1) = -0.785398
    c: DistanceY(g2) = 20
    c: Angle(g3) = -2.35619
FEATURE [Sketcher::SketchObject] Sketch037  label="BumpTrim"
  FullyConstrained = false
  MapMode = 5
  sketch-geometry (4):
    g0: LineSegment StartX=-26.2848 StartY=31.2083 StartZ=0 EndX=-1.26106 EndY=31.2083 EndZ=0
    g1: LineSegment StartX=-1.26106 StartY=31.2083 StartZ=0 EndX=-1.26106 EndY=20 EndZ=0
    g2: LineSegment StartX=-1.26106 StartY=20 StartZ=0 EndX=-26.2848 EndY=20 EndZ=0
    g3: LineSegment StartX=-26.2848 StartY=20 StartZ=0 EndX=-26.2848 EndY=31.2083 EndZ=0
  constraints (9):
    c: Coincident(g0,g1)
    c: Coincident(g1,g2)
    c: Coincident(g2,g3)
    c: Coincident(g3,g0)
    c: Horizontal(g0)
    c: Horizontal(g2)
    c: Vertical(g1)
    c: Vertical(g3)
    c: DistanceY(g1) = 20
FEATURE [PartDesign::Pocket] Pocket011
  BaseFeature = -> Pocket010
  Length = 10
  Length2 = 100
  Profile = -> Sketch003
  Type = 0
FEATURE [Sketcher::SketchObject] Sketch036  label="countersink"
  FullyConstrained = true
  MapMode = 5
  Support = -> [Pocket011]
  sketch-geometry (14):
    g0: LineSegment StartX=11.9037 StartY=-8.546 StartZ=0 EndX=10.8577 EndY=-4.64226 EndZ=0
    g1: LineSegment StartX=10.8577 StartY=-4.64226 StartZ=0 EndX=6.954 EndY=-3.59626 EndZ=0
    g2: LineSegment StartX=6.954 StartY=-3.59626 StartZ=0 EndX=4.09626 EndY=-6.454 EndZ=0
    g3: LineSegment StartX=4.09626 StartY=-6.454 StartZ=0 EndX=5.14226 EndY=-10.3577 EndZ=0
    g4: LineSegment StartX=5.14226 StartY=-10.3577 StartZ=0 EndX=9.046 EndY=-11.4037 EndZ=0
    g5: LineSegment StartX=9.046 StartY=-11.4037 StartZ=0 EndX=11.9037 EndY=-8.546 EndZ=0
    g6: Circle CenterX=8 CenterY=-7.5 CenterZ=0 NormalX=0 NormalY=0 NormalZ=1 AngleXU=0 Radius=4.04145
    g7: LineSegment StartX=-5.14226 StartY=-4.64226 StartZ=0 EndX=-9.046 EndY=-3.59626 EndZ=0
    g8: LineSegment StartX=-9.046 StartY=-3.59626 StartZ=0 EndX=-11.9037 EndY=-6.454 EndZ=0
    g9: LineSegment StartX=-11.9037 StartY=-6.454 StartZ=0 EndX=-10.8577 EndY=-10.3577 EndZ=0
    g10: LineSegment StartX=-10.8577 StartY=-10.3577 StartZ=0 EndX=-6.954 EndY=-11.4037 EndZ=0
    g11: LineSegment StartX=-6.954 StartY=-11.4037 StartZ=0 EndX=-4.09626 EndY=-8.546 EndZ=0
    g12: LineSegment StartX=-4.09626 StartY=-8.546 StartZ=0 EndX=-5.14226 EndY=-4.64226 EndZ=0
    g13: Circle CenterX=-8 CenterY=-7.5 CenterZ=0 NormalX=0 NormalY=0 NormalZ=1 AngleXU=0 Radius=4.04145
  constraints (34):
    c: Coincident(g0,g1)
    c: Coincident(g1,g2)
    c: Coincident(g2,g3)
    c: Coincident(g3,g4)
    c: Coincident(g4,g5)
    c: Coincident(g5,g0)
    c: Equal(g0, g1-g5) x5
    c: PointOnObject(g0,g6)
    c: PointOnObject(g1,g6)
    c: PointOnObject(g2,g6)
    c: PointOnObject(g3,g6)
    c: PointOnObject(g4,g6)
    c: PointOnObject(g5,g6)
    c: Coincident(g7,g8)
    c: Coincident(g8,g9)
    c: Coincident(g9,g10)
    c: Coincident(g10,g11)
    c: Coincident(g11,g12)
    c: Coincident(g12,g7)
    c: Equal(g7, g8-g12) x5
    c: PointOnObject(g7,g13)
    c: PointOnObject(g8,g13)
    c: PointOnObject(g9,g13)
    c: PointOnObject(g10,g13)
    c: PointOnObject(g11,g13)
    c: PointOnObject(g12,g13)
    c: Angle(g11) = 0.785398
    c: Angle(g5) = 0.785398
    c: Distance(g0,g2) = 7
    c: Distance(g7,g8) = 7
    c: DistanceX(g6) = 8
    c: DistanceY(g6) = -7.5
    c: DistanceY(g13) = -7.5
    c: DistanceX(g13) = -8
FEATURE [PartDesign::Pocket] Pocket012
  BaseFeature = -> Pocket011
  Length = 3
  Length2 = 100
  Profile = -> Sketch036
  Type = 0
FEATURE [PartDesign::Pocket] Pocket013
  BaseFeature = -> Pocket012
  Length = 5
  Length2 = 100
  Profile = -> Sketch033
  Type = 0
FEATURE [PartDesign::Pad] Pad002
  BaseFeature = -> Pocket013
  Direction = (1,1,1)
  Length = 3
  Length2 = 100
  Profile = -> Sketch035
  Reversed = true
  Type = 0
FEATURE [PartDesign::Pocket] Pocket014
  BaseFeature = -> Pad002
  Length = 40
  Length2 = 100
  Profile = -> Sketch037
  Type = 0
FEATURE [PartDesign::Pad] Pad003
  BaseFeature = -> Pocket014
  Direction = (1,1,1)
  Length = 10
  Length2 = 100
  Profile = -> Sketch029
  Type = 0
FEATURE [Sketcher::SketchObject] Sketch039  label="platformBump"
  ExternalGeometry = -> [Pad003]
  FullyConstrained = true
  MapMode = 5
  Support = -> [Pad003]
  sketch-geometry (4):
    g0: LineSegment StartX=-30.6621 StartY=23.5355 StartZ=0 EndX=12.2218 EndY=23.5355 EndZ=0
    g1: LineSegment StartX=12.2218 StartY=23.5355 StartZ=0 EndX=15.7574 EndY=20 EndZ=0
    g2: LineSegment StartX=15.7574 StartY=20 StartZ=0 EndX=-34.1976 EndY=20 EndZ=0
    g3: LineSegment StartX=-34.1976 StartY=20 StartZ=0 EndX=-30.6621 EndY=23.5355 EndZ=0
  constraints (10):
    c: Coincident(g0,g1)
    c: Coincident(g1,g2)
    c: Coincident(g2,g3)
    c: Coincident(g3,g0)
    c: Horizontal(g0)
    c: Distance(g1) = 5
    c: Coincident(g2,g-3)
    c: Coincident(g1,g-4)
    c: Angle(g1) = -0.785398
    c: Angle(g3) = 0.785398
FEATURE [PartDesign::Pad] Pad004
  BaseFeature = -> Pad003
  Direction = (1,1,1)
  Length = 4
  Length2 = 100
  Profile = -> Sketch039
  Reversed = true
  Type = 0
FEATURE [Sketcher::SketchObject] Sketch040  label="WireHoles"
  FullyConstrained = true
  MapMode = 5
  Support = -> [Pad004]
  sketch-geometry (21):
    g0: LineSegment StartX=16.1911 StartY=-17.3989 StartZ=0 EndX=17.49 EndY=-15.8509 EndZ=0
    g1: LineSegment StartX=17.49 StartY=-15.8509 StartZ=0 EndX=16.7989 EndY=-13.952 EndZ=0
    g2: LineSegment StartX=16.7989 StartY=-13.952 StartZ=0 EndX=14.8089 EndY=-13.6011 EndZ=0
    g3: LineSegment StartX=14.8089 StartY=-13.6011 StartZ=0 EndX=13.51 EndY=-15.1491 EndZ=0
    g4: LineSegment StartX=13.51 StartY=-15.1491 StartZ=0 EndX=14.2011 EndY=-17.048 EndZ=0
    g5: LineSegment StartX=14.2011 StartY=-17.048 StartZ=0 EndX=16.1911 EndY=-17.3989 EndZ=0
    g6: Circle CenterX=15.5 CenterY=-15.5 CenterZ=0 NormalX=0 NormalY=0 NormalZ=1 AngleXU=0 Radius=2.02073
    g7: LineSegment StartX=14.977 StartY=17.4519 StartZ=0 EndX=13.5481 EndY=16.023 EndZ=0
    g8: LineSegment StartX=13.5481 StartY=16.023 StartZ=0 EndX=14.0711 EndY=14.0711 EndZ=0
    g9: LineSegment StartX=14.0711 StartY=14.0711 StartZ=0 EndX=16.023 EndY=13.5481 EndZ=0
    g10: LineSegment StartX=16.023 StartY=13.5481 StartZ=0 EndX=17.4519 EndY=14.977 EndZ=0
    g11: LineSegment StartX=17.4519 StartY=14.977 StartZ=0 EndX=16.9289 EndY=16.9289 EndZ=0
    g12: LineSegment StartX=16.9289 StartY=16.9289 StartZ=0 EndX=14.977 EndY=17.4519 EndZ=0
    g13: Circle CenterX=15.5 CenterY=15.5 CenterZ=0 NormalX=0 NormalY=0 NormalZ=1 AngleXU=0 Radius=2.02073
    g14: LineSegment StartX=-14.7753 StartY=-17.2247 StartZ=0 EndX=-14.327 EndY=-15.5517 EndZ=0
    g15: LineSegment StartX=-14.327 StartY=-15.5517 StartZ=0 EndX=-15.5517 EndY=-14.327 EndZ=0
    g16: LineSegment StartX=-15.5517 StartY=-14.327 StartZ=0 EndX=-17.2247 EndY=-14.7753 EndZ=0
    g17: LineSegment StartX=-17.2247 StartY=-14.7753 StartZ=0 EndX=-17.673 EndY=-16.4483 EndZ=0
    g18: LineSegment StartX=-17.673 StartY=-16.4483 StartZ=0 EndX=-16.4483 EndY=-17.673 EndZ=0
    g19: LineSegment StartX=-16.4483 StartY=-17.673 StartZ=0 EndX=-14.7753 EndY=-17.2247 EndZ=0
    g20: Circle CenterX=-16 CenterY=-16 CenterZ=0 NormalX=0 NormalY=0 NormalZ=1 AngleXU=0 Radius=1.73205
  constraints (51):
    c: Coincident(g0,g1)
    c: Coincident(g1,g2)
    c: Coincident(g2,g3)
    c: Coincident(g3,g4)
    c: Coincident(g4,g5)
    c: Coincident(g5,g0)
    c: Equal(g0, g1-g5) x5
    c: PointOnObject(g0,g6)
    c: PointOnObject(g1,g6)
    c: PointOnObject(g2,g6)
    c: PointOnObject(g3,g6)
    c: PointOnObject(g4,g6)
    c: PointOnObject(g5,g6)
    c: Coincident(g7,g8)
    c: Coincident(g8,g9)
    c: Coincident(g9,g10)
    c: Coincident(g10,g11)
    c: Coincident(g11,g12)
    c: Coincident(g12,g7)
    c: Equal(g7, g8-g12) x5
    c: PointOnObject(g7,g13)
    c: PointOnObject(g8,g13)
    c: PointOnObject(g9,g13)
    c: PointOnObject(g10,g13)
    c: PointOnObject(g11,g13)
    c: PointOnObject(g12,g13)
    c: Distance(g0,g4) = 3.5
    c: Distance(g7,g11) = 3.5
    c: DistanceX(g13) = 15.5
    c: DistanceY(g13) = 15.5
    c: DistanceX(g6) = 15.5
    c: DistanceY(g6) = -15.5
    c: Coincident(g14,g15)
    c: Coincident(g15,g16)
    c: Coincident(g16,g17)
    c: Coincident(g17,g18)
    c: Coincident(g18,g19)
    c: Coincident(g19,g14)
    c: Equal(g14, g15-g19) x5
    c: PointOnObject(g14,g20)
    c: PointOnObject(g15,g20)
    c: PointOnObject(g16,g20)
    c: PointOnObject(g17,g20)
    c: PointOnObject(g18,g20)
    c: PointOnObject(g19,g20)
    c: Distance(g18,g14) = 3
    c: Angle(g15) = 2.35619
    c: DistanceX(g20) = -16
    c: DistanceY(g20) = -16
    c: Angle(g3) = -2.26893
    c: Angle(g11) = 1.8326
FEATURE [PartDesign::Pocket] Pocket015
  BaseFeature = -> Pad004
  Length = 5
  Length2 = 100
  Profile = -> Sketch040
  Type = 1
FEATURE [Sketcher::SketchObject] Sketch041  label="PCBmountholes"
  FullyConstrained = true
  MapMode = 5
  Placement = pos=(-3.00001,-9.80387e-07,0) rot=(0.57735,0.57735,0.57735;2.0944rad)
  Support = -> [Pocket015]
  sketch-geometry (2):
    g0: Circle CenterX=16 CenterY=-34 CenterZ=0 NormalX=0 NormalY=0 NormalZ=1 AngleXU=0 Radius=1.15
    g1: Circle CenterX=-16 CenterY=-34 CenterZ=0 NormalX=0 NormalY=0 NormalZ=1 AngleXU=0 Radius=1.15
  constraints (5):
    c: Distance(g0,g1) = 32
    c: Symmetric(g1,g0,g-2)
    c: Diameter(g0) = 2.3
    c: Equal(g0,g1)
    c: DistanceY(g1) = -34
FEATURE [PartDesign::Pocket] Pocket016
  BaseFeature = -> Pocket015
  Length = 5
  Length2 = 100
  Profile = -> Sketch041
  Type = 0
FEATURE [Sketcher::SketchObject] Sketch042
  FullyConstrained = true
  MapMode = 5
  Placement = pos=(0,0,-53) rot=(1,0,0;3.14159rad)
  Support = -> [Pocket014]
  sketch-geometry (7):
    g0: LineSegment StartX=-13.3547 StartY=-12.2 StartZ=0 EndX=-12.7774 EndY=-13.2 EndZ=0
    g1: LineSegment StartX=-12.7774 StartY=-13.2 StartZ=0 EndX=-11.6226 EndY=-13.2 EndZ=0
    g2: LineSegment StartX=-11.6226 StartY=-13.2 StartZ=0 EndX=-11.0453 EndY=-12.2 EndZ=0
    g3: LineSegment StartX=-11.0453 StartY=-12.2 StartZ=0 EndX=-11.6226 EndY=-11.2 EndZ=0
    g4: LineSegment StartX=-11.6226 StartY=-11.2 StartZ=0 EndX=-12.7774 EndY=-11.2 EndZ=0
    g5: LineSegment StartX=-12.7774 StartY=-11.2 StartZ=0 EndX=-13.3547 EndY=-12.2 EndZ=0
    g6: Circle CenterX=-12.2 CenterY=-12.2 CenterZ=0 NormalX=0 NormalY=0 NormalZ=1 AngleXU=0 Radius=1.1547
  constraints (17):
    c: Coincident(g0,g1)
    c: Coincident(g1,g2)
    c: Coincident(g2,g3)
    c: Coincident(g3,g4)
    c: Coincident(g4,g5)
    c: Coincident(g5,g0)
    c: Equal(g0, g1-g5) x5
    c: PointOnObject(g0,g6)
    c: PointOnObject(g1,g6)
    c: PointOnObject(g2,g6)
    c: PointOnObject(g3,g6)
    c: PointOnObject(g4,g6)
    c: PointOnObject(g5,g6)
    c: DistanceX(g6) = -12.2
    c: DistanceY(g6) = -12.2
    c: Distance(g0,g4) = 2
    c: Angle(g1) = 0
FEATURE [PartDesign::Pocket] Pocket017
  BaseFeature = -> Pocket016
  Length = 5
  Length2 = 100
  Profile = -> Sketch042
  Type = 1
FEATURE [Sketcher::SketchObject] Sketch043
  FullyConstrained = true
  MapMode = 5
  Support = -> [Pocket017]
  sketch-geometry (1):
    g0: Circle CenterX=-12.2 CenterY=12.2 CenterZ=0 NormalX=0 NormalY=0 NormalZ=1 AngleXU=0 Radius=2.125
  constraints (3):
    c: DistanceX(g0) = -12.2
    c: DistanceY(g0) = 12.2
    c: Diameter(g0) = 4.25
FEATURE [PartDesign::Pocket] Pocket018
  BaseFeature = -> Pocket017
  Length = 18
  Length2 = 100
  Profile = -> Sketch043
  Type = 0
FEATURE [PartDesign::Body] Body
  Group = -> [Sketch,Pad,Sketch001,Pocket,Sketch003,Sketch004,Sketch007,Sketch008,Sketch009,Sketch010,Sketch017,Sketch019,Sketch021,Pocket002,Sketch022,Sketch024,Sketch025,Sketch026,Pocket003,Pocket004,Pocket005,Pocket006,Pocket007,Pocket008,Pad001,Pocket009,Pocket010,Sketch029,Sketch033,Sketch035,Sketch036,Sketch037,Pocket011,Pocket012,Pocket013,Pad002,Pocket014,Pad003,Sketch039,Pad004,Sketch040,Pocket015,+6 more]
  Origin = -> Origin
  Placement = pos=(0,0,0) rot=(0.862856,-0.357407,0.357407;1.71777rad)
  Tip = -> Pocket018
FEATURE [Mesh::Feature] Mesh  label="Pocket018 (Meshed)"
